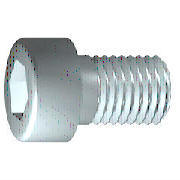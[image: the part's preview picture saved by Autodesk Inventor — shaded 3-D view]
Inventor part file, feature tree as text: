
AUTODESK INVENTOR PART (.ipt)
format: ipt  version: 2024.2 (Build 282272000, 272)  size: 198,144 bytes
history: native  units: mm (DEFAULTED — no unit token found)
features: extrude x1, plane x1, fillet x1
ambient origin geometry x7: Origin, YZ Plane, XY Plane, X Axis, Y Axis, Z Axis, Center Point
bodies: Solid1 (feature_tree), Body (feature_tree)
feature tree (3):
  extrude  "Slot"  Depth=3.875mm
  plane  "Work Plane1"
  fillet  "Fillet2"  Radius=0.276153mm
